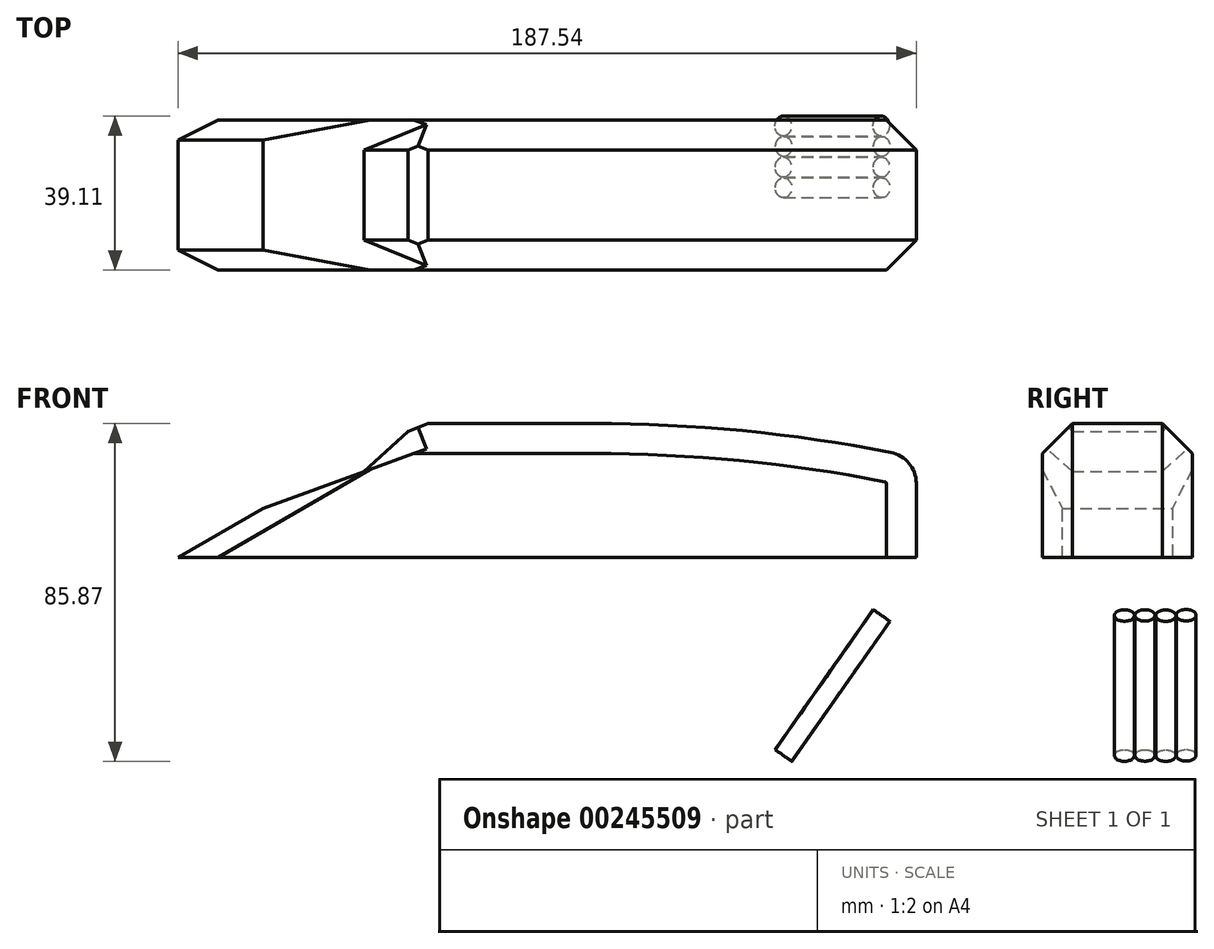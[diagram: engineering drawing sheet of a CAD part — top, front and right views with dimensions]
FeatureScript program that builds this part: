
annotation { "Feature Type Name" : "Feature", "Feature Type Description" : "" }
export const myFeature = defineFeature(function(context is Context, id is Id, definition is map)
    precondition{}
    {
        {
            var Q0;
            Q0=qCreatedBy(makeId("Front.planeOp"),FACE);
            var sketch = newSketch(context, id + "F0", { "sketchPlane" : qUnion([Q0])});
            skLineSegment(sketch, "E0", {"start": v(-138.63, 0) * mm, "end": v(-117.03, 12.52) * mm});
            skLineSegment(sketch, "E1", {"start": v(-117.03, 12.52) * mm, "end": v(-91.41, 21.83) * mm});
            skLineSegment(sketch, "E2", {"start": v(-91.41, 21.83) * mm, "end": v(-78.02, 34.06) * mm});
            skLineSegment(sketch, "E3", {"start": v(-78.02, 34.06) * mm, "end": v(20.38, 34.06) * mm});
            skLineSegment(sketch, "E4", {"start": v(20.38, 34.06) * mm, "end": v(48.9, 25.4) * mm});
            skLineSegment(sketch, "E5", {"start": v(48.9, 25.4) * mm, "end": v(48.9, 0) * mm});
            skLineSegment(sketch, "E6", {"start": v(48.9, 0) * mm, "end": v(0, 0) * mm});
            skLineSegment(sketch, "E7", {"start": v(0, 0) * mm, "end": v(-54.15, 0) * mm});
            skLineSegment(sketch, "E8", {"start": v(-54.15, 0) * mm, "end": v(-86.75, 0) * mm});
            skLineSegment(sketch, "E9", {"start": v(-86.75, 0) * mm, "end": v(-138.63, 0) * mm});
            skLineSegment(sketch, "E10", {"start": v(-28.82, 34.06) * mm, "end": v(-58.22, 34.06) * mm});
            skLineSegment(sketch, "E11", {"start": v(-58.22, 34.06) * mm, "end": v(0, 34.06) * mm});
            skSolve(sketch);
        }
        {
            var Q0;
            Q0 = qSketchRegion(id + "F0", true);
            extrude(context, id + "F1", {"entities" : qUnion([Q0]), "depth" : 38.1 * mm});
        }
        {
            var Q0;
            Q0=makeQuery(id+"F1.opExtrude","SWEPT_EDGE",EDGE,{"disambiguationData":[OSD([sQuery(id+"F0.wireOp",EDGE,"E3"),sQuery(id+"F0.wireOp",EDGE,"E4")])]});
            fillet(context, id + "F2", {"entities" : qUnion([Q0]), "radius" : 394.07 * mm, "tangentPropagation" : true, "allowEdgeOverflow" : false});
        }
        {
            var Q0;
            Q0=makeQuery(id+"F2.opFillet","BLEND_EDGE",EDGE,{"blendedFrom":[makeQuery(id+"F1.opExtrude","SWEPT_EDGE",EDGE,{"disambiguationData":[OSD([sQuery(id+"F0.wireOp",EDGE,"E3"),sQuery(id+"F0.wireOp",EDGE,"E4")])]}),makeQuery(id+"F1.opExtrude","SWEPT_FACE",FACE,{"disambiguationData":[OSD([sQuery(id+"F0.wireOp",EDGE,"E5")])]})],"blendedInto":[makeQuery(id+"F1.opExtrude","SWEPT_FACE",FACE,{"disambiguationData":[OSD([sQuery(id+"F0.wireOp",EDGE,"E5")])]})]});
            fillet(context, id + "F3", {"entities" : qUnion([Q0]), "radius" : 7.98 * mm, "tangentPropagation" : true, "allowEdgeOverflow" : false});
        }
        {
            var Q0;
            Q0=makeQuery(id+"F1.opExtrude","CAP_EDGE",EDGE,{"disambiguationData":[OSD([sQuery(id+"F0.wireOp",EDGE,"E2")])],"isStart":false});
            var Q1;
            Q1=makeQuery(id+"F1.opExtrude","CAP_EDGE",EDGE,{"disambiguationData":[OSD([sQuery(id+"F0.wireOp",EDGE,"E2")])],"isStart":true});
            var Q2;
            Q2=makeQuery(id+"F1.opExtrude","SWEPT_EDGE",EDGE,{"disambiguationData":[OSD([sQuery(id+"F0.wireOp",EDGE,"E2"),sQuery(id+"F0.wireOp",EDGE,"E3")])]});
            chamfer(context, id + "F4", {"entities" : qUnion([Q0, Q1, Q2]), "width" : 7.62 * mm, "tangentPropagation" : true});
        }
        {
            var Q0;
            Q0=makeQuery(id+"F1.opExtrude","CAP_EDGE",EDGE,{"disambiguationData":[OSD([sQuery(id+"F0.wireOp",EDGE,"E0")])],"isStart":false});
            var Q1;
            Q1=makeQuery(id+"F1.opExtrude","CAP_EDGE",EDGE,{"disambiguationData":[OSD([sQuery(id+"F0.wireOp",EDGE,"E0")])],"isStart":true});
            chamfer(context, id + "F5", {"entities" : qUnion([Q0, Q1]), "width" : 5.08 * mm, "tangentPropagation" : true});
        }
        {
            var Q0;
            Q0=makeQuery(id+"F1.opExtrude","CAP_EDGE",EDGE,{"disambiguationData":[OSD([sQuery(id+"F0.wireOp",EDGE,"E3"),sQuery(id+"F0.wireOp",EDGE,"E11")])],"isStart":false});
            var Q1;
            Q1=makeQuery(id+"F1.opExtrude","CAP_EDGE",EDGE,{"disambiguationData":[OSD([sQuery(id+"F0.wireOp",EDGE,"E3"),sQuery(id+"F0.wireOp",EDGE,"E11")])],"isStart":true});
            chamfer(context, id + "F6", {"entities" : qUnion([Q0, Q1]), "width" : 7.62 * mm, "tangentPropagation" : true});
        }
        {
            var Q0;
            Q0=qCreatedBy(makeId("Right.planeOp"),FACE);
            var Q1;
            {var subQ0=sQuery(id+"F0.wireOp",EDGE,"E4");var subQ1=sQuery(id+"F0.wireOp",EDGE,"E3");Q1=makeQuery(id+"F3.opFillet","BLEND_EDGE",EDGE,{"blendedFrom":[makeQuery(id+"F2.opFillet","BLEND_EDGE",EDGE,{"blendedFrom":[makeQuery(id+"F1.opExtrude","SWEPT_EDGE",EDGE,{"disambiguationData":[OSD([subQ1,subQ0])]}),makeQuery(id+"F1.opExtrude","SWEPT_FACE",FACE,{"disambiguationData":[OSD([sQuery(id+"F0.wireOp",EDGE,"E5")])]})],"blendedInto":[makeQuery(id+"F1.opExtrude","SWEPT_FACE",FACE,{"disambiguationData":[OSD([sQuery(id+"F0.wireOp",EDGE,"E5")])]})]}),makeQuery(id+"F2.opFillet","BLEND_FACE",FACE,{"disambiguationData":[OSD([subQ1,subQ0])]})],"blendedInto":[makeQuery(id+"F2.opFillet","BLEND_FACE",FACE,{"disambiguationData":[OSD([subQ1,subQ0])]})]});}
            cPlane(context, id + "F7", {"entities" : qUnion([Q0, Q1]), "cplaneType" : CPlaneType.LINE_ANGLE, "offset" : 25.4 * mm, "angle" : 55 * degree, "oppositeDirection" : true, "width" : 152.4 * mm, "height" : 152.4 * mm});
        }
        {
            var Q0;
            Q0=qCreatedBy(id+"F7.planeOp",FACE);
            var sketch = newSketch(context, id + "F8", { "sketchPlane" : qUnion([Q0])});
            skCircle(sketch, "E12", {"center": v(41.19, 1.53) * mm, "radius": 2.54 * mm});
            skCircle(sketch, "E13", {"center": v(41.37, 6.7) * mm, "radius": 2.54 * mm});
            skCircle(sketch, "E14", {"center": v(41.26, 11.99) * mm, "radius": 2.54 * mm});
            skCircle(sketch, "E15", {"center": v(41.3, 17.22) * mm, "radius": 2.54 * mm});
            skSolve(sketch);
        }
        {
            var Q0;
            Q0 = qSketchRegion(id + "F8", true);
            extrude(context, id + "F9", {"entities" : qUnion([Q0]), "depth" : 78.74 * mm, "hasSecondDirection" : true, "secondDirectionOppositeDirection" : false, "secondDirectionDepth" : 35.3 * mm});
        }
        {
            var Q0;
            Q0=qCreatedBy(makeId("Front.planeOp"),FACE);
            var sketch = newSketch(context, id + "F10", { "sketchPlane" : qUnion([Q0])});
            skCircle(sketch, "E16", {"center": v(-84.31, 5.05) * mm, "radius": 2.24 * mm});
            skCircle(sketch, "E17", {"center": v(19.87, 7.4) * mm, "radius": 2.57 * mm});
            skSolve(sketch);
        }
        {
            var Q0;
            Q0 = qSketchRegion(id + "F10", true);
            extrude(context, id + "F11", {"entities" : qUnion([Q0]), "operationType" : NewBodyOperationType.REMOVE, "oppositeDirection" : true, "depth" : 25.4 * mm});
        }
    });
